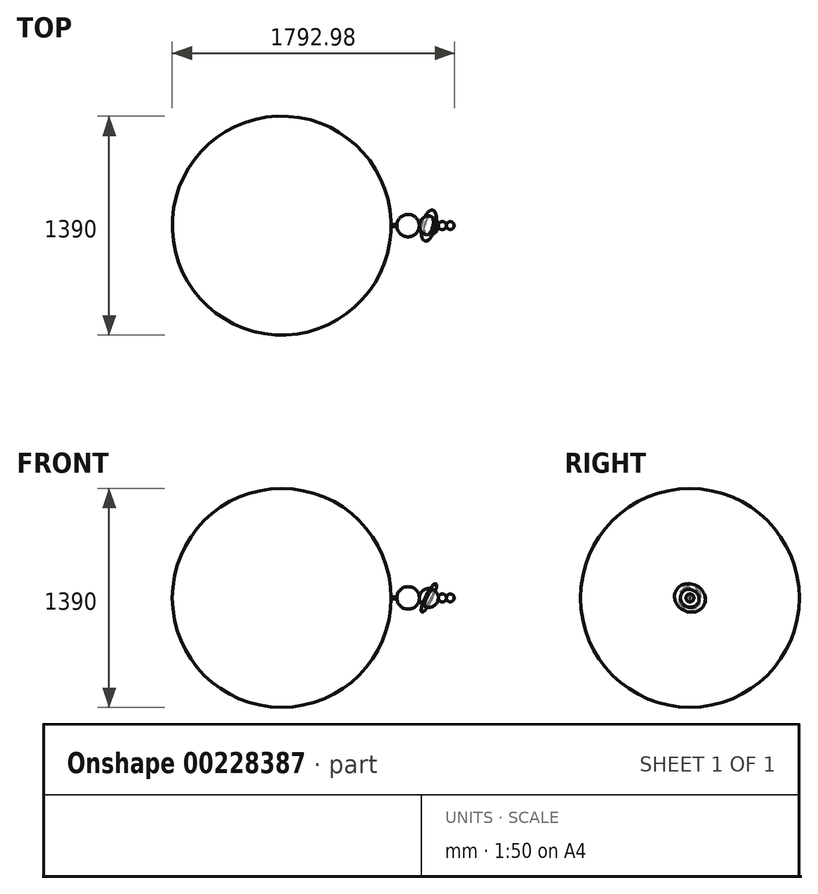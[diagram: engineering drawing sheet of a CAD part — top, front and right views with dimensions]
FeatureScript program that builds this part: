
annotation { "Feature Type Name" : "Feature", "Feature Type Description" : "" }
export const myFeature = defineFeature(function(context is Context, id is Id, definition is map)
    precondition{}
    {
        {
            assignVariable(context, id + "F0", {"name" : "SunD", "anyValue" : 1390});
        }
        {
            assignVariable(context, id + "F1", {"name" : "MercuryD", "anyValue" : 4.88});
        }
        {
            assignVariable(context, id + "F2", {"name" : "VenusD", "anyValue" : 12.1});
        }
        {
            assignVariable(context, id + "F3", {"name" : "EarthD", "anyValue" : 12.76});
        }
        {
            assignVariable(context, id + "F4", {"name" : "MarsD", "anyValue" : 6.8});
        }
        {
            assignVariable(context, id + "F5", {"name" : "JupiterD", "anyValue" : 143});
        }
        {
            assignVariable(context, id + "F6", {"name" : "SaturnD", "anyValue" : 120.5});
        }
        {
            assignVariable(context, id + "F7", {"name" : "UranusD", "anyValue" : 51.1});
        }
        {
            assignVariable(context, id + "F8", {"name" : "NeptuneD", "anyValue" : 49.5});
        }
        {
            assignVariable(context, id + "F9", {"name" : "PlutoD", "anyValue" : 2.35});
        }
        {
            var Q0;
            Q0=qCreatedBy(makeId("Top.planeOp"),FACE);
            var sketch = newSketch(context, id + "F10", { "sketchPlane" : qUnion([Q0])});
            skCircle(sketch, "E0", {"center": v(0, 0) * mm, "radius": 695 * mm});
            skCircle(sketch, "E1", {"center": v(0, 0) * mm, "radius": 2.44 * mm});
            skCircle(sketch, "E2", {"center": v(0, 0) * mm, "radius": 6.05 * mm});
            skCircle(sketch, "E3", {"center": v(0, 0) * mm, "radius": 6.38 * mm});
            skCircle(sketch, "E4", {"center": v(0, 0) * mm, "radius": 3.4 * mm});
            skCircle(sketch, "E5", {"center": v(0, 0) * mm, "radius": 71.5 * mm});
            skCircle(sketch, "E6", {"center": v(0, 0) * mm, "radius": 60.25 * mm});
            skCircle(sketch, "E7", {"center": v(0, 0) * mm, "radius": 25.55 * mm});
            skCircle(sketch, "E8", {"center": v(0, 0) * mm, "radius": 24.75 * mm});
            skCircle(sketch, "E9", {"center": v(0, 0) * mm, "radius": 1.18 * mm});
            skLineSegment(sketch, "E10", {"start": v(-694.4, -28.81) * mm, "end": v(0, 0) * mm});
            skLineSegment(sketch, "E11", {"start": v(0, 0) * mm, "end": v(694.4, 28.81) * mm});
            skCircle(sketch, "E12", {"center": v(0, 0) * mm, "radius": 100.25 * mm});
            skLineSegment(sketch, "E13", {"start": v(0, 0) * mm, "end": v(-4.16, 100.16) * mm, "construction": true});
            skSolve(sketch);
        }
        {
            var Q0;
            {var subQ0=sQuery(id+"F10.wireOp",EDGE,"E10");var subQ1=sQuery(id+"F10.wireOp",EDGE,"E1");var subQ2=makeQuery(id+"F10.imprint","INTERSECT",VERTEX,{"derivedFrom":[subQ1,subQ0]});Q0=makeQuery(id+"F10.imprint","IMPRINT",FACE,{"disambiguationData":[TD([[makeQuery(id+"F10.imprint","IMPRINT",EDGE,{"disambiguationData":[TD([[subQ2,1.0]])],"derivedFrom":subQ1}),1.0]])]});}
            var Q1;
            {var subQ0=sQuery(id+"F10.wireOp",EDGE,"E10");var subQ1=sQuery(id+"F10.wireOp",EDGE,"E9");var subQ2=makeQuery(id+"F10.imprint","INTERSECT",VERTEX,{"derivedFrom":[subQ1,subQ0]});Q1=makeQuery(id+"F10.imprint","IMPRINT",FACE,{"disambiguationData":[TD([[makeQuery(id+"F10.imprint","IMPRINT",EDGE,{"disambiguationData":[TD([[subQ2,1.0]])],"derivedFrom":subQ1}),1.0]])]});}
            var Q2;
            Q2=sQuery(id+"F10.wireOp",EDGE,"E10");
            revolve(context, id + "F11", {"entities" : qUnion([Q0, Q1]), "axis" : qUnion([Q2]), "revolveType" : RevolveType.FULL});
        }
        {
            var Q0;
            Q0=makeQuery(id+"F11.opRevolve","SWEPT_BODY",BODY,{"disambiguationData":[OSD([sQuery(id+"F10.wireOp",EDGE,"E1"),sQuery(id+"F10.wireOp",EDGE,"E10"),sQuery(id+"F10.wireOp",EDGE,"E11")])]});
            transform(context, id + "F12", {"entities" : qUnion([Q0]), "transformType" : TransformType.TRANSLATION_3D, "dx" : (getVariable(context, 'SunD') / 2 + getVariable(context, 'MercuryD') / 2) * mm, "dy" : 0 * mm, "dz" : 0 * mm, "makeCopy" : false});
        }
        {
            var Q0;
            {var subQ0=sQuery(id+"F10.wireOp",EDGE,"E10");var subQ1=sQuery(id+"F10.wireOp",EDGE,"E2");var subQ2=makeQuery(id+"F10.imprint","INTERSECT",VERTEX,{"derivedFrom":[subQ1,subQ0]});Q0=makeQuery(id+"F10.imprint","IMPRINT",FACE,{"disambiguationData":[TD([[makeQuery(id+"F10.imprint","IMPRINT",EDGE,{"disambiguationData":[TD([[subQ2,1.0]])],"derivedFrom":subQ1}),1.0]])]});}
            var Q1;
            {var subQ0=sQuery(id+"F10.wireOp",EDGE,"E10");var subQ1=sQuery(id+"F10.wireOp",EDGE,"E1");var subQ2=makeQuery(id+"F10.imprint","INTERSECT",VERTEX,{"derivedFrom":[subQ1,subQ0]});Q1=makeQuery(id+"F10.imprint","IMPRINT",FACE,{"disambiguationData":[TD([[makeQuery(id+"F10.imprint","IMPRINT",EDGE,{"disambiguationData":[TD([[subQ2,1.0]])],"derivedFrom":subQ1}),-1.0]])]});}
            var Q2;
            {var subQ0=sQuery(id+"F10.wireOp",EDGE,"E10");var subQ1=sQuery(id+"F10.wireOp",EDGE,"E1");var subQ2=makeQuery(id+"F10.imprint","INTERSECT",VERTEX,{"derivedFrom":[subQ1,subQ0]});Q2=makeQuery(id+"F10.imprint","IMPRINT",FACE,{"disambiguationData":[TD([[makeQuery(id+"F10.imprint","IMPRINT",EDGE,{"disambiguationData":[TD([[subQ2,1.0]])],"derivedFrom":subQ1}),1.0]])]});}
            var Q3;
            {var subQ0=sQuery(id+"F10.wireOp",EDGE,"E10");var subQ1=sQuery(id+"F10.wireOp",EDGE,"E9");var subQ2=makeQuery(id+"F10.imprint","INTERSECT",VERTEX,{"derivedFrom":[subQ1,subQ0]});Q3=makeQuery(id+"F10.imprint","IMPRINT",FACE,{"disambiguationData":[TD([[makeQuery(id+"F10.imprint","IMPRINT",EDGE,{"disambiguationData":[TD([[subQ2,1.0]])],"derivedFrom":subQ1}),1.0]])]});}
            var Q4;
            Q4=sQuery(id+"F10.wireOp",EDGE,"E11");
            revolve(context, id + "F13", {"entities" : qUnion([Q0, Q1, Q2, Q3]), "axis" : qUnion([Q4]), "revolveType" : RevolveType.FULL});
        }
        {
            var Q0;
            Q0=makeQuery(id+"F13.opRevolve","SWEPT_BODY",BODY,{"disambiguationData":[OSD([sQuery(id+"F10.wireOp",EDGE,"E2"),sQuery(id+"F10.wireOp",EDGE,"E10"),sQuery(id+"F10.wireOp",EDGE,"E11")])]});
            transform(context, id + "F14", {"entities" : qUnion([Q0]), "transformType" : TransformType.TRANSLATION_3D, "dx" : (getVariable(context, 'SunD') / 2 + getVariable(context, 'MercuryD') + getVariable(context, 'VenusD') / 2) * mm, "dy" : 0 * mm, "dz" : 0 * mm, "makeCopy" : false});
        }
        {
            var Q0;
            {var subQ0=sQuery(id+"F10.wireOp",EDGE,"E10");var subQ1=sQuery(id+"F10.wireOp",EDGE,"E2");var subQ2=makeQuery(id+"F10.imprint","INTERSECT",VERTEX,{"derivedFrom":[subQ1,subQ0]});Q0=makeQuery(id+"F10.imprint","IMPRINT",FACE,{"disambiguationData":[TD([[makeQuery(id+"F10.imprint","IMPRINT",EDGE,{"disambiguationData":[TD([[subQ2,1.0]])],"derivedFrom":subQ1}),-1.0]])]});}
            var Q1;
            {var subQ0=sQuery(id+"F10.wireOp",EDGE,"E10");var subQ1=sQuery(id+"F10.wireOp",EDGE,"E2");var subQ2=makeQuery(id+"F10.imprint","INTERSECT",VERTEX,{"derivedFrom":[subQ1,subQ0]});Q1=makeQuery(id+"F10.imprint","IMPRINT",FACE,{"disambiguationData":[TD([[makeQuery(id+"F10.imprint","IMPRINT",EDGE,{"disambiguationData":[TD([[subQ2,1.0]])],"derivedFrom":subQ1}),1.0]])]});}
            var Q2;
            {var subQ0=sQuery(id+"F10.wireOp",EDGE,"E10");var subQ1=sQuery(id+"F10.wireOp",EDGE,"E1");var subQ2=makeQuery(id+"F10.imprint","INTERSECT",VERTEX,{"derivedFrom":[subQ1,subQ0]});Q2=makeQuery(id+"F10.imprint","IMPRINT",FACE,{"disambiguationData":[TD([[makeQuery(id+"F10.imprint","IMPRINT",EDGE,{"disambiguationData":[TD([[subQ2,1.0]])],"derivedFrom":subQ1}),-1.0]])]});}
            var Q3;
            {var subQ0=sQuery(id+"F10.wireOp",EDGE,"E10");var subQ1=sQuery(id+"F10.wireOp",EDGE,"E1");var subQ2=makeQuery(id+"F10.imprint","INTERSECT",VERTEX,{"derivedFrom":[subQ1,subQ0]});Q3=makeQuery(id+"F10.imprint","IMPRINT",FACE,{"disambiguationData":[TD([[makeQuery(id+"F10.imprint","IMPRINT",EDGE,{"disambiguationData":[TD([[subQ2,1.0]])],"derivedFrom":subQ1}),1.0]])]});}
            var Q4;
            {var subQ0=sQuery(id+"F10.wireOp",EDGE,"E10");var subQ1=sQuery(id+"F10.wireOp",EDGE,"E9");var subQ2=makeQuery(id+"F10.imprint","INTERSECT",VERTEX,{"derivedFrom":[subQ1,subQ0]});Q4=makeQuery(id+"F10.imprint","IMPRINT",FACE,{"disambiguationData":[TD([[makeQuery(id+"F10.imprint","IMPRINT",EDGE,{"disambiguationData":[TD([[subQ2,1.0]])],"derivedFrom":subQ1}),1.0]])]});}
            var Q5;
            Q5=sQuery(id+"F10.wireOp",EDGE,"E10");
            revolve(context, id + "F15", {"entities" : qUnion([Q0, Q1, Q2, Q3, Q4]), "axis" : qUnion([Q5]), "revolveType" : RevolveType.FULL});
        }
        {
            var Q0;
            Q0=makeQuery(id+"F15.opRevolve","SWEPT_BODY",BODY,{"disambiguationData":[OSD([sQuery(id+"F10.wireOp",EDGE,"E3"),sQuery(id+"F10.wireOp",EDGE,"E10"),sQuery(id+"F10.wireOp",EDGE,"E11")])]});
            transform(context, id + "F16", {"entities" : qUnion([Q0]), "transformType" : TransformType.TRANSLATION_3D, "dx" : (getVariable(context, 'SunD') / 2 + getVariable(context, 'MercuryD') + getVariable(context, 'VenusD') + getVariable(context, 'EarthD') / 2) * mm, "dy" : 0 * mm, "dz" : 0 * mm, "makeCopy" : false});
        }
        {
            var Q0;
            {var subQ0=sQuery(id+"F10.wireOp",EDGE,"E10");var subQ1=sQuery(id+"F10.wireOp",EDGE,"E1");var subQ2=makeQuery(id+"F10.imprint","INTERSECT",VERTEX,{"derivedFrom":[subQ1,subQ0]});Q0=makeQuery(id+"F10.imprint","IMPRINT",FACE,{"disambiguationData":[TD([[makeQuery(id+"F10.imprint","IMPRINT",EDGE,{"disambiguationData":[TD([[subQ2,1.0]])],"derivedFrom":subQ1}),-1.0]])]});}
            var Q1;
            {var subQ0=sQuery(id+"F10.wireOp",EDGE,"E10");var subQ1=sQuery(id+"F10.wireOp",EDGE,"E1");var subQ2=makeQuery(id+"F10.imprint","INTERSECT",VERTEX,{"derivedFrom":[subQ1,subQ0]});Q1=makeQuery(id+"F10.imprint","IMPRINT",FACE,{"disambiguationData":[TD([[makeQuery(id+"F10.imprint","IMPRINT",EDGE,{"disambiguationData":[TD([[subQ2,1.0]])],"derivedFrom":subQ1}),1.0]])]});}
            var Q2;
            {var subQ0=sQuery(id+"F10.wireOp",EDGE,"E10");var subQ1=sQuery(id+"F10.wireOp",EDGE,"E9");var subQ2=makeQuery(id+"F10.imprint","INTERSECT",VERTEX,{"derivedFrom":[subQ1,subQ0]});Q2=makeQuery(id+"F10.imprint","IMPRINT",FACE,{"disambiguationData":[TD([[makeQuery(id+"F10.imprint","IMPRINT",EDGE,{"disambiguationData":[TD([[subQ2,1.0]])],"derivedFrom":subQ1}),1.0]])]});}
            var Q3;
            Q3=sQuery(id+"F10.wireOp",EDGE,"E11");
            revolve(context, id + "F17", {"entities" : qUnion([Q0, Q1, Q2]), "axis" : qUnion([Q3]), "revolveType" : RevolveType.FULL});
        }
        {
            var Q0;
            Q0=makeQuery(id+"F17.opRevolve","SWEPT_BODY",BODY,{"disambiguationData":[OSD([sQuery(id+"F10.wireOp",EDGE,"E4"),sQuery(id+"F10.wireOp",EDGE,"E10"),sQuery(id+"F10.wireOp",EDGE,"E11")])]});
            transform(context, id + "F18", {"entities" : qUnion([Q0]), "transformType" : TransformType.TRANSLATION_3D, "dx" : (getVariable(context, 'SunD') / 2 + getVariable(context, 'MercuryD') + getVariable(context, 'VenusD') + getVariable(context, 'EarthD') + getVariable(context, 'MarsD') / 2) * mm, "dy" : 0 * mm, "dz" : 0 * mm, "makeCopy" : false});
        }
        {
            var Q0;
            {var subQ0=sQuery(id+"F10.wireOp",EDGE,"E10");var subQ1=sQuery(id+"F10.wireOp",EDGE,"E5");var subQ2=makeQuery(id+"F10.imprint","INTERSECT",VERTEX,{"derivedFrom":[subQ1,subQ0]});Q0=makeQuery(id+"F10.imprint","IMPRINT",FACE,{"disambiguationData":[TD([[makeQuery(id+"F10.imprint","IMPRINT",EDGE,{"disambiguationData":[TD([[subQ2,1.0]])],"derivedFrom":subQ1}),1.0]])]});}
            var Q1;
            {var subQ0=sQuery(id+"F10.wireOp",EDGE,"E10");var subQ1=sQuery(id+"F10.wireOp",EDGE,"E6");var subQ2=makeQuery(id+"F10.imprint","INTERSECT",VERTEX,{"derivedFrom":[subQ1,subQ0]});Q1=makeQuery(id+"F10.imprint","IMPRINT",FACE,{"disambiguationData":[TD([[makeQuery(id+"F10.imprint","IMPRINT",EDGE,{"disambiguationData":[TD([[subQ2,1.0]])],"derivedFrom":subQ1}),1.0]])]});}
            var Q2;
            {var subQ0=sQuery(id+"F10.wireOp",EDGE,"E10");var subQ1=sQuery(id+"F10.wireOp",EDGE,"E3");var subQ2=makeQuery(id+"F10.imprint","INTERSECT",VERTEX,{"derivedFrom":[subQ1,subQ0]});Q2=makeQuery(id+"F10.imprint","IMPRINT",FACE,{"disambiguationData":[TD([[makeQuery(id+"F10.imprint","IMPRINT",EDGE,{"disambiguationData":[TD([[subQ2,1.0]])],"derivedFrom":subQ1}),-1.0]])]});}
            var Q3;
            {var subQ0=sQuery(id+"F10.wireOp",EDGE,"E10");var subQ1=sQuery(id+"F10.wireOp",EDGE,"E7");var subQ2=makeQuery(id+"F10.imprint","INTERSECT",VERTEX,{"derivedFrom":[subQ1,subQ0]});Q3=makeQuery(id+"F10.imprint","IMPRINT",FACE,{"disambiguationData":[TD([[makeQuery(id+"F10.imprint","IMPRINT",EDGE,{"disambiguationData":[TD([[subQ2,1.0]])],"derivedFrom":subQ1}),1.0]])]});}
            var Q4;
            {var subQ0=sQuery(id+"F10.wireOp",EDGE,"E10");var subQ1=sQuery(id+"F10.wireOp",EDGE,"E2");var subQ2=makeQuery(id+"F10.imprint","INTERSECT",VERTEX,{"derivedFrom":[subQ1,subQ0]});Q4=makeQuery(id+"F10.imprint","IMPRINT",FACE,{"disambiguationData":[TD([[makeQuery(id+"F10.imprint","IMPRINT",EDGE,{"disambiguationData":[TD([[subQ2,1.0]])],"derivedFrom":subQ1}),1.0]])]});}
            var Q5;
            {var subQ0=sQuery(id+"F10.wireOp",EDGE,"E10");var subQ1=sQuery(id+"F10.wireOp",EDGE,"E1");var subQ2=makeQuery(id+"F10.imprint","INTERSECT",VERTEX,{"derivedFrom":[subQ1,subQ0]});Q5=makeQuery(id+"F10.imprint","IMPRINT",FACE,{"disambiguationData":[TD([[makeQuery(id+"F10.imprint","IMPRINT",EDGE,{"disambiguationData":[TD([[subQ2,1.0]])],"derivedFrom":subQ1}),-1.0]])]});}
            var Q6;
            {var subQ0=sQuery(id+"F10.wireOp",EDGE,"E10");var subQ1=sQuery(id+"F10.wireOp",EDGE,"E1");var subQ2=makeQuery(id+"F10.imprint","INTERSECT",VERTEX,{"derivedFrom":[subQ1,subQ0]});Q6=makeQuery(id+"F10.imprint","IMPRINT",FACE,{"disambiguationData":[TD([[makeQuery(id+"F10.imprint","IMPRINT",EDGE,{"disambiguationData":[TD([[subQ2,1.0]])],"derivedFrom":subQ1}),1.0]])]});}
            var Q7;
            {var subQ0=sQuery(id+"F10.wireOp",EDGE,"E10");var subQ1=sQuery(id+"F10.wireOp",EDGE,"E9");var subQ2=makeQuery(id+"F10.imprint","INTERSECT",VERTEX,{"derivedFrom":[subQ1,subQ0]});Q7=makeQuery(id+"F10.imprint","IMPRINT",FACE,{"disambiguationData":[TD([[makeQuery(id+"F10.imprint","IMPRINT",EDGE,{"disambiguationData":[TD([[subQ2,1.0]])],"derivedFrom":subQ1}),1.0]])]});}
            var Q8;
            {var subQ0=sQuery(id+"F10.wireOp",EDGE,"E10");var subQ1=sQuery(id+"F10.wireOp",EDGE,"E2");var subQ2=makeQuery(id+"F10.imprint","INTERSECT",VERTEX,{"derivedFrom":[subQ1,subQ0]});Q8=makeQuery(id+"F10.imprint","IMPRINT",FACE,{"disambiguationData":[TD([[makeQuery(id+"F10.imprint","IMPRINT",EDGE,{"disambiguationData":[TD([[subQ2,1.0]])],"derivedFrom":subQ1}),-1.0]])]});}
            var Q9;
            Q9=sQuery(id+"F10.wireOp",EDGE,"E11");
            revolve(context, id + "F19", {"entities" : qUnion([Q0, Q1, Q2, Q3, Q4, Q5, Q6, Q7, Q8]), "axis" : qUnion([Q9]), "revolveType" : RevolveType.FULL});
        }
        {
            var Q0;
            Q0=makeQuery(id+"F19.opRevolve","SWEPT_BODY",BODY,{"disambiguationData":[OSD([sQuery(id+"F10.wireOp",EDGE,"E5"),sQuery(id+"F10.wireOp",EDGE,"E10"),sQuery(id+"F10.wireOp",EDGE,"E11")])]});
            transform(context, id + "F20", {"entities" : qUnion([Q0]), "transformType" : TransformType.TRANSLATION_3D, "dx" : (getVariable(context, 'SunD') / 2 + getVariable(context, 'MercuryD') + getVariable(context, 'VenusD') + getVariable(context, 'EarthD') + getVariable(context, 'MarsD') + getVariable(context, 'JupiterD') / 2) * mm, "dy" : 0 * mm, "dz" : 0 * mm, "makeCopy" : false});
        }
        {
            var Q0;
            {var subQ0=sQuery(id+"F10.wireOp",EDGE,"E10");var subQ1=sQuery(id+"F10.wireOp",EDGE,"E6");var subQ2=makeQuery(id+"F10.imprint","INTERSECT",VERTEX,{"derivedFrom":[subQ1,subQ0]});Q0=makeQuery(id+"F10.imprint","IMPRINT",FACE,{"disambiguationData":[TD([[makeQuery(id+"F10.imprint","IMPRINT",EDGE,{"disambiguationData":[TD([[subQ2,1.0]])],"derivedFrom":subQ1}),1.0]])]});}
            var Q1;
            {var subQ0=sQuery(id+"F10.wireOp",EDGE,"E10");var subQ1=sQuery(id+"F10.wireOp",EDGE,"E7");var subQ2=makeQuery(id+"F10.imprint","INTERSECT",VERTEX,{"derivedFrom":[subQ1,subQ0]});Q1=makeQuery(id+"F10.imprint","IMPRINT",FACE,{"disambiguationData":[TD([[makeQuery(id+"F10.imprint","IMPRINT",EDGE,{"disambiguationData":[TD([[subQ2,1.0]])],"derivedFrom":subQ1}),1.0]])]});}
            var Q2;
            {var subQ0=sQuery(id+"F10.wireOp",EDGE,"E10");var subQ1=sQuery(id+"F10.wireOp",EDGE,"E3");var subQ2=makeQuery(id+"F10.imprint","INTERSECT",VERTEX,{"derivedFrom":[subQ1,subQ0]});Q2=makeQuery(id+"F10.imprint","IMPRINT",FACE,{"disambiguationData":[TD([[makeQuery(id+"F10.imprint","IMPRINT",EDGE,{"disambiguationData":[TD([[subQ2,1.0]])],"derivedFrom":subQ1}),-1.0]])]});}
            var Q3;
            {var subQ0=sQuery(id+"F10.wireOp",EDGE,"E10");var subQ1=sQuery(id+"F10.wireOp",EDGE,"E2");var subQ2=makeQuery(id+"F10.imprint","INTERSECT",VERTEX,{"derivedFrom":[subQ1,subQ0]});Q3=makeQuery(id+"F10.imprint","IMPRINT",FACE,{"disambiguationData":[TD([[makeQuery(id+"F10.imprint","IMPRINT",EDGE,{"disambiguationData":[TD([[subQ2,1.0]])],"derivedFrom":subQ1}),1.0]])]});}
            var Q4;
            {var subQ0=sQuery(id+"F10.wireOp",EDGE,"E10");var subQ1=sQuery(id+"F10.wireOp",EDGE,"E1");var subQ2=makeQuery(id+"F10.imprint","INTERSECT",VERTEX,{"derivedFrom":[subQ1,subQ0]});Q4=makeQuery(id+"F10.imprint","IMPRINT",FACE,{"disambiguationData":[TD([[makeQuery(id+"F10.imprint","IMPRINT",EDGE,{"disambiguationData":[TD([[subQ2,1.0]])],"derivedFrom":subQ1}),-1.0]])]});}
            var Q5;
            {var subQ0=sQuery(id+"F10.wireOp",EDGE,"E10");var subQ1=sQuery(id+"F10.wireOp",EDGE,"E1");var subQ2=makeQuery(id+"F10.imprint","INTERSECT",VERTEX,{"derivedFrom":[subQ1,subQ0]});Q5=makeQuery(id+"F10.imprint","IMPRINT",FACE,{"disambiguationData":[TD([[makeQuery(id+"F10.imprint","IMPRINT",EDGE,{"disambiguationData":[TD([[subQ2,1.0]])],"derivedFrom":subQ1}),1.0]])]});}
            var Q6;
            {var subQ0=sQuery(id+"F10.wireOp",EDGE,"E10");var subQ1=sQuery(id+"F10.wireOp",EDGE,"E9");var subQ2=makeQuery(id+"F10.imprint","INTERSECT",VERTEX,{"derivedFrom":[subQ1,subQ0]});Q6=makeQuery(id+"F10.imprint","IMPRINT",FACE,{"disambiguationData":[TD([[makeQuery(id+"F10.imprint","IMPRINT",EDGE,{"disambiguationData":[TD([[subQ2,1.0]])],"derivedFrom":subQ1}),1.0]])]});}
            var Q7;
            {var subQ0=sQuery(id+"F10.wireOp",EDGE,"E10");var subQ1=sQuery(id+"F10.wireOp",EDGE,"E2");var subQ2=makeQuery(id+"F10.imprint","INTERSECT",VERTEX,{"derivedFrom":[subQ1,subQ0]});Q7=makeQuery(id+"F10.imprint","IMPRINT",FACE,{"disambiguationData":[TD([[makeQuery(id+"F10.imprint","IMPRINT",EDGE,{"disambiguationData":[TD([[subQ2,1.0]])],"derivedFrom":subQ1}),-1.0]])]});}
            var Q8;
            Q8=sQuery(id+"F10.wireOp",EDGE,"E10");
            revolve(context, id + "F21", {"entities" : qUnion([Q0, Q1, Q2, Q3, Q4, Q5, Q6, Q7]), "axis" : qUnion([Q8]), "revolveType" : RevolveType.FULL});
        }
        {
            var Q0;
            {var subQ0=sQuery(id+"F10.wireOp",EDGE,"E10");var subQ1=sQuery(id+"F10.wireOp",EDGE,"E5");var subQ2=makeQuery(id+"F10.imprint","INTERSECT",VERTEX,{"derivedFrom":[subQ1,subQ0]});Q0=makeQuery(id+"F10.imprint","IMPRINT",FACE,{"disambiguationData":[TD([[makeQuery(id+"F10.imprint","IMPRINT",EDGE,{"disambiguationData":[TD([[subQ2,1.0]])],"derivedFrom":subQ1}),-1.0]])]});}
            var Q1;
            {var subQ0=sQuery(id+"F10.wireOp",EDGE,"E10");var subQ1=sQuery(id+"F10.wireOp",EDGE,"E5");var subQ2=makeQuery(id+"F10.imprint","INTERSECT",VERTEX,{"derivedFrom":[subQ1,subQ0]});Q1=makeQuery(id+"F10.imprint","IMPRINT",FACE,{"disambiguationData":[TD([[makeQuery(id+"F10.imprint","IMPRINT",EDGE,{"disambiguationData":[TD([[subQ2,1.0]])],"derivedFrom":subQ1}),1.0]])]});}
            var Q2;
            {var subQ0=sQuery(id+"F10.wireOp",EDGE,"E10");var subQ1=sQuery(id+"F10.wireOp",EDGE,"E5");var subQ2=makeQuery(id+"F10.imprint","INTERSECT",VERTEX,{"derivedFrom":[subQ1,subQ0]});Q2=makeQuery(id+"F10.imprint","IMPRINT",FACE,{"disambiguationData":[TD([[makeQuery(id+"F10.imprint","IMPRINT",EDGE,{"disambiguationData":[TD([[subQ2,-1.0]])],"derivedFrom":subQ1}),1.0]])]});}
            var Q3;
            {var subQ0=sQuery(id+"F10.wireOp",EDGE,"E10");var subQ1=sQuery(id+"F10.wireOp",EDGE,"E5");var subQ2=makeQuery(id+"F10.imprint","INTERSECT",VERTEX,{"derivedFrom":[subQ1,subQ0]});Q3=makeQuery(id+"F10.imprint","IMPRINT",FACE,{"disambiguationData":[TD([[makeQuery(id+"F10.imprint","IMPRINT",EDGE,{"disambiguationData":[TD([[subQ2,-1.0]])],"derivedFrom":subQ1}),-1.0]])]});}
            extrude(context, id + "F22", {"entities" : qUnion([Q0, Q1, Q2, Q3]), "operationType" : NewBodyOperationType.ADD, "depth" : 0.5 * mm});
        }
        {
            var Q0;
            {var subQ0=sQuery(id+"F10.wireOp",EDGE,"E10");var subQ1=sQuery(id+"F10.wireOp",EDGE,"E5");var subQ2=makeQuery(id+"F10.imprint","INTERSECT",VERTEX,{"derivedFrom":[subQ1,subQ0]});Q0=makeQuery(id+"F10.imprint","IMPRINT",FACE,{"disambiguationData":[TD([[makeQuery(id+"F10.imprint","IMPRINT",EDGE,{"disambiguationData":[TD([[subQ2,1.0]])],"derivedFrom":subQ1}),-1.0]])]});}
            var Q1;
            {var subQ0=sQuery(id+"F10.wireOp",EDGE,"E10");var subQ1=sQuery(id+"F10.wireOp",EDGE,"E5");var subQ2=makeQuery(id+"F10.imprint","INTERSECT",VERTEX,{"derivedFrom":[subQ1,subQ0]});Q1=makeQuery(id+"F10.imprint","IMPRINT",FACE,{"disambiguationData":[TD([[makeQuery(id+"F10.imprint","IMPRINT",EDGE,{"disambiguationData":[TD([[subQ2,1.0]])],"derivedFrom":subQ1}),1.0]])]});}
            var Q2;
            {var subQ0=sQuery(id+"F10.wireOp",EDGE,"E10");var subQ1=sQuery(id+"F10.wireOp",EDGE,"E5");var subQ2=makeQuery(id+"F10.imprint","INTERSECT",VERTEX,{"derivedFrom":[subQ1,subQ0]});Q2=makeQuery(id+"F10.imprint","IMPRINT",FACE,{"disambiguationData":[TD([[makeQuery(id+"F10.imprint","IMPRINT",EDGE,{"disambiguationData":[TD([[subQ2,-1.0]])],"derivedFrom":subQ1}),-1.0]])]});}
            var Q3;
            {var subQ0=sQuery(id+"F10.wireOp",EDGE,"E10");var subQ1=sQuery(id+"F10.wireOp",EDGE,"E5");var subQ2=makeQuery(id+"F10.imprint","INTERSECT",VERTEX,{"derivedFrom":[subQ1,subQ0]});Q3=makeQuery(id+"F10.imprint","IMPRINT",FACE,{"disambiguationData":[TD([[makeQuery(id+"F10.imprint","IMPRINT",EDGE,{"disambiguationData":[TD([[subQ2,-1.0]])],"derivedFrom":subQ1}),1.0]])]});}
            extrude(context, id + "F23", {"entities" : qUnion([Q0, Q1, Q2, Q3]), "operationType" : NewBodyOperationType.ADD, "oppositeDirection" : true, "depth" : 0.5 * mm});
        }
        {
            var Q0;
            Q0=makeQuery(id+"F21.opRevolve","SWEPT_BODY",BODY,{"disambiguationData":[OSD([sQuery(id+"F10.wireOp",EDGE,"E6"),sQuery(id+"F10.wireOp",EDGE,"E10"),sQuery(id+"F10.wireOp",EDGE,"E11")])]});
            var Q1;
            Q1=sQuery(id+"F10.wireOp",EDGE,"E13");
            transform(context, id + "F24", {"entities" : qUnion([Q0]), "transformType" : TransformType.ROTATION, "transformAxis" : qUnion([Q1]), "angle" : 120 * degree, "makeCopy" : false});
        }
        {
            var Q0;
            Q0=makeQuery(id+"F21.opRevolve","SWEPT_BODY",BODY,{"disambiguationData":[OSD([sQuery(id+"F10.wireOp",EDGE,"E6"),sQuery(id+"F10.wireOp",EDGE,"E10"),sQuery(id+"F10.wireOp",EDGE,"E11")])]});
            var Q1;
            Q1=sQuery(id+"F10.wireOp",EDGE,"E10");
            transform(context, id + "F25", {"entities" : qUnion([Q0]), "transformType" : TransformType.ROTATION, "transformAxis" : qUnion([Q1]), "angle" : 30 * degree, "oppositeDirection" : true, "makeCopy" : false});
        }
        {
            var Q0;
            Q0=makeQuery(id+"F21.opRevolve","SWEPT_BODY",BODY,{"disambiguationData":[OSD([sQuery(id+"F10.wireOp",EDGE,"E6"),sQuery(id+"F10.wireOp",EDGE,"E10"),sQuery(id+"F10.wireOp",EDGE,"E11")])]});
            transform(context, id + "F26", {"entities" : qUnion([Q0]), "transformType" : TransformType.TRANSLATION_3D, "dx" : (getVariable(context, 'SunD') / 2 + getVariable(context, 'MercuryD') + getVariable(context, 'VenusD') + getVariable(context, 'EarthD') + getVariable(context, 'MarsD') + getVariable(context, 'JupiterD') + getVariable(context, 'SaturnD') / 2) * mm, "dy" : 0 * mm, "dz" : 0 * mm, "makeCopy" : false});
        }
        {
            var Q0;
            {var subQ0=sQuery(id+"F10.wireOp",EDGE,"E10");var subQ1=sQuery(id+"F10.wireOp",EDGE,"E3");var subQ2=makeQuery(id+"F10.imprint","INTERSECT",VERTEX,{"derivedFrom":[subQ1,subQ0]});Q0=makeQuery(id+"F10.imprint","IMPRINT",FACE,{"disambiguationData":[TD([[makeQuery(id+"F10.imprint","IMPRINT",EDGE,{"disambiguationData":[TD([[subQ2,1.0]])],"derivedFrom":subQ1}),-1.0]])]});}
            var Q1;
            {var subQ0=sQuery(id+"F10.wireOp",EDGE,"E10");var subQ1=sQuery(id+"F10.wireOp",EDGE,"E2");var subQ2=makeQuery(id+"F10.imprint","INTERSECT",VERTEX,{"derivedFrom":[subQ1,subQ0]});Q1=makeQuery(id+"F10.imprint","IMPRINT",FACE,{"disambiguationData":[TD([[makeQuery(id+"F10.imprint","IMPRINT",EDGE,{"disambiguationData":[TD([[subQ2,1.0]])],"derivedFrom":subQ1}),1.0]])]});}
            var Q2;
            {var subQ0=sQuery(id+"F10.wireOp",EDGE,"E10");var subQ1=sQuery(id+"F10.wireOp",EDGE,"E1");var subQ2=makeQuery(id+"F10.imprint","INTERSECT",VERTEX,{"derivedFrom":[subQ1,subQ0]});Q2=makeQuery(id+"F10.imprint","IMPRINT",FACE,{"disambiguationData":[TD([[makeQuery(id+"F10.imprint","IMPRINT",EDGE,{"disambiguationData":[TD([[subQ2,1.0]])],"derivedFrom":subQ1}),-1.0]])]});}
            var Q3;
            {var subQ0=sQuery(id+"F10.wireOp",EDGE,"E10");var subQ1=sQuery(id+"F10.wireOp",EDGE,"E1");var subQ2=makeQuery(id+"F10.imprint","INTERSECT",VERTEX,{"derivedFrom":[subQ1,subQ0]});Q3=makeQuery(id+"F10.imprint","IMPRINT",FACE,{"disambiguationData":[TD([[makeQuery(id+"F10.imprint","IMPRINT",EDGE,{"disambiguationData":[TD([[subQ2,1.0]])],"derivedFrom":subQ1}),1.0]])]});}
            var Q4;
            {var subQ0=sQuery(id+"F10.wireOp",EDGE,"E10");var subQ1=sQuery(id+"F10.wireOp",EDGE,"E9");var subQ2=makeQuery(id+"F10.imprint","INTERSECT",VERTEX,{"derivedFrom":[subQ1,subQ0]});Q4=makeQuery(id+"F10.imprint","IMPRINT",FACE,{"disambiguationData":[TD([[makeQuery(id+"F10.imprint","IMPRINT",EDGE,{"disambiguationData":[TD([[subQ2,1.0]])],"derivedFrom":subQ1}),1.0]])]});}
            var Q5;
            {var subQ0=sQuery(id+"F10.wireOp",EDGE,"E10");var subQ1=sQuery(id+"F10.wireOp",EDGE,"E2");var subQ2=makeQuery(id+"F10.imprint","INTERSECT",VERTEX,{"derivedFrom":[subQ1,subQ0]});Q5=makeQuery(id+"F10.imprint","IMPRINT",FACE,{"disambiguationData":[TD([[makeQuery(id+"F10.imprint","IMPRINT",EDGE,{"disambiguationData":[TD([[subQ2,1.0]])],"derivedFrom":subQ1}),-1.0]])]});}
            var Q6;
            {var subQ0=sQuery(id+"F10.wireOp",EDGE,"E10");var subQ1=sQuery(id+"F10.wireOp",EDGE,"E7");var subQ2=makeQuery(id+"F10.imprint","INTERSECT",VERTEX,{"derivedFrom":[subQ1,subQ0]});Q6=makeQuery(id+"F10.imprint","IMPRINT",FACE,{"disambiguationData":[TD([[makeQuery(id+"F10.imprint","IMPRINT",EDGE,{"disambiguationData":[TD([[subQ2,1.0]])],"derivedFrom":subQ1}),1.0]])]});}
            var Q7;
            Q7=sQuery(id+"F10.wireOp",EDGE,"E10");
            revolve(context, id + "F27", {"entities" : qUnion([Q0, Q1, Q2, Q3, Q4, Q5, Q6]), "axis" : qUnion([Q7]), "revolveType" : RevolveType.FULL});
        }
        {
            var Q0;
            Q0=makeQuery(id+"F27.opRevolve","SWEPT_BODY",BODY,{"disambiguationData":[OSD([sQuery(id+"F10.wireOp",EDGE,"E7"),sQuery(id+"F10.wireOp",EDGE,"E10"),sQuery(id+"F10.wireOp",EDGE,"E11")])]});
            transform(context, id + "F28", {"entities" : qUnion([Q0]), "transformType" : TransformType.TRANSLATION_3D, "dx" : (getVariable(context, 'SunD') / 2 + getVariable(context, 'MercuryD') + getVariable(context, 'VenusD') + getVariable(context, 'EarthD') + getVariable(context, 'MarsD') + getVariable(context, 'JupiterD') + getVariable(context, 'SaturnD') + getVariable(context, 'UranusD') / 2) * mm, "dy" : 0 * mm, "dz" : 0 * mm, "makeCopy" : false});
        }
        {
            var Q0;
            {var subQ0=sQuery(id+"F10.wireOp",EDGE,"E10");var subQ1=sQuery(id+"F10.wireOp",EDGE,"E9");var subQ2=makeQuery(id+"F10.imprint","INTERSECT",VERTEX,{"derivedFrom":[subQ1,subQ0]});Q0=makeQuery(id+"F10.imprint","IMPRINT",FACE,{"disambiguationData":[TD([[makeQuery(id+"F10.imprint","IMPRINT",EDGE,{"disambiguationData":[TD([[subQ2,1.0]])],"derivedFrom":subQ1}),1.0]])]});}
            var Q1;
            {var subQ0=sQuery(id+"F10.wireOp",EDGE,"E10");var subQ1=sQuery(id+"F10.wireOp",EDGE,"E1");var subQ2=makeQuery(id+"F10.imprint","INTERSECT",VERTEX,{"derivedFrom":[subQ1,subQ0]});Q1=makeQuery(id+"F10.imprint","IMPRINT",FACE,{"disambiguationData":[TD([[makeQuery(id+"F10.imprint","IMPRINT",EDGE,{"disambiguationData":[TD([[subQ2,1.0]])],"derivedFrom":subQ1}),1.0]])]});}
            var Q2;
            {var subQ0=sQuery(id+"F10.wireOp",EDGE,"E10");var subQ1=sQuery(id+"F10.wireOp",EDGE,"E1");var subQ2=makeQuery(id+"F10.imprint","INTERSECT",VERTEX,{"derivedFrom":[subQ1,subQ0]});Q2=makeQuery(id+"F10.imprint","IMPRINT",FACE,{"disambiguationData":[TD([[makeQuery(id+"F10.imprint","IMPRINT",EDGE,{"disambiguationData":[TD([[subQ2,1.0]])],"derivedFrom":subQ1}),-1.0]])]});}
            var Q3;
            {var subQ0=sQuery(id+"F10.wireOp",EDGE,"E10");var subQ1=sQuery(id+"F10.wireOp",EDGE,"E2");var subQ2=makeQuery(id+"F10.imprint","INTERSECT",VERTEX,{"derivedFrom":[subQ1,subQ0]});Q3=makeQuery(id+"F10.imprint","IMPRINT",FACE,{"disambiguationData":[TD([[makeQuery(id+"F10.imprint","IMPRINT",EDGE,{"disambiguationData":[TD([[subQ2,1.0]])],"derivedFrom":subQ1}),1.0]])]});}
            var Q4;
            {var subQ0=sQuery(id+"F10.wireOp",EDGE,"E10");var subQ1=sQuery(id+"F10.wireOp",EDGE,"E2");var subQ2=makeQuery(id+"F10.imprint","INTERSECT",VERTEX,{"derivedFrom":[subQ1,subQ0]});Q4=makeQuery(id+"F10.imprint","IMPRINT",FACE,{"disambiguationData":[TD([[makeQuery(id+"F10.imprint","IMPRINT",EDGE,{"disambiguationData":[TD([[subQ2,1.0]])],"derivedFrom":subQ1}),-1.0]])]});}
            var Q5;
            {var subQ0=sQuery(id+"F10.wireOp",EDGE,"E10");var subQ1=sQuery(id+"F10.wireOp",EDGE,"E3");var subQ2=makeQuery(id+"F10.imprint","INTERSECT",VERTEX,{"derivedFrom":[subQ1,subQ0]});Q5=makeQuery(id+"F10.imprint","IMPRINT",FACE,{"disambiguationData":[TD([[makeQuery(id+"F10.imprint","IMPRINT",EDGE,{"disambiguationData":[TD([[subQ2,1.0]])],"derivedFrom":subQ1}),-1.0]])]});}
            var Q6;
            Q6=sQuery(id+"F10.wireOp",EDGE,"E10");
            revolve(context, id + "F29", {"entities" : qUnion([Q0, Q1, Q2, Q3, Q4, Q5]), "axis" : qUnion([Q6]), "revolveType" : RevolveType.FULL});
        }
        {
            var Q0;
            Q0=makeQuery(id+"F29.opRevolve","SWEPT_BODY",BODY,{"disambiguationData":[OSD([sQuery(id+"F10.wireOp",EDGE,"E8"),sQuery(id+"F10.wireOp",EDGE,"E10"),sQuery(id+"F10.wireOp",EDGE,"E11")])]});
            transform(context, id + "F30", {"entities" : qUnion([Q0]), "transformType" : TransformType.TRANSLATION_3D, "dx" : (getVariable(context, 'SunD') / 2 + getVariable(context, 'MercuryD') + getVariable(context, 'VenusD') + getVariable(context, 'EarthD') + getVariable(context, 'MarsD') + getVariable(context, 'JupiterD') + getVariable(context, 'SaturnD') + getVariable(context, 'UranusD') + getVariable(context, 'NeptuneD') / 2) * mm, "dy" : 0 * mm, "dz" : 0 * mm, "makeCopy" : false});
        }
        {
            var Q0;
            {var subQ0=sQuery(id+"F10.wireOp",EDGE,"E10");var subQ1=sQuery(id+"F10.wireOp",EDGE,"E9");var subQ2=makeQuery(id+"F10.imprint","INTERSECT",VERTEX,{"derivedFrom":[subQ1,subQ0]});Q0=makeQuery(id+"F10.imprint","IMPRINT",FACE,{"disambiguationData":[TD([[makeQuery(id+"F10.imprint","IMPRINT",EDGE,{"disambiguationData":[TD([[subQ2,1.0]])],"derivedFrom":subQ1}),1.0]])]});}
            var Q1;
            Q1=sQuery(id+"F10.wireOp",EDGE,"E10");
            revolve(context, id + "F31", {"entities" : qUnion([Q0]), "axis" : qUnion([Q1]), "revolveType" : RevolveType.FULL});
        }
        {
            var Q0;
            Q0=makeQuery(id+"F31.opRevolve","SWEPT_BODY",BODY,{"disambiguationData":[OSD([sQuery(id+"F10.wireOp",EDGE,"E9"),sQuery(id+"F10.wireOp",EDGE,"E10"),sQuery(id+"F10.wireOp",EDGE,"E11")])]});
            transform(context, id + "F32", {"entities" : qUnion([Q0]), "transformType" : TransformType.TRANSLATION_3D, "dx" : (getVariable(context, 'SunD') / 2 + getVariable(context, 'MercuryD') + getVariable(context, 'VenusD') + getVariable(context, 'EarthD') + getVariable(context, 'MarsD') + getVariable(context, 'JupiterD') + getVariable(context, 'SaturnD') + getVariable(context, 'UranusD') + getVariable(context, 'NeptuneD') + getVariable(context, 'PlutoD') / 2) * mm, "dy" : 0 * mm, "dz" : 0 * mm, "makeCopy" : false});
        }
        {
            var Q0;
            {var subQ0=sQuery(id+"F10.wireOp",EDGE,"E10");var subQ1=sQuery(id+"F10.wireOp",EDGE,"E0");var subQ2=makeQuery(id+"F10.imprint","INTERSECT",VERTEX,{"derivedFrom":[subQ1,subQ0]});Q0=makeQuery(id+"F10.imprint","IMPRINT",FACE,{"disambiguationData":[TD([[makeQuery(id+"F10.imprint","IMPRINT",EDGE,{"disambiguationData":[TD([[subQ2,1.0]])],"derivedFrom":subQ1}),1.0]])]});}
            var Q1;
            {var subQ0=sQuery(id+"F10.wireOp",EDGE,"E10");var subQ1=sQuery(id+"F10.wireOp",EDGE,"E5");var subQ2=makeQuery(id+"F10.imprint","INTERSECT",VERTEX,{"derivedFrom":[subQ1,subQ0]});Q1=makeQuery(id+"F10.imprint","IMPRINT",FACE,{"disambiguationData":[TD([[makeQuery(id+"F10.imprint","IMPRINT",EDGE,{"disambiguationData":[TD([[subQ2,1.0]])],"derivedFrom":subQ1}),-1.0]])]});}
            var Q2;
            {var subQ0=sQuery(id+"F10.wireOp",EDGE,"E10");var subQ1=sQuery(id+"F10.wireOp",EDGE,"E5");var subQ2=makeQuery(id+"F10.imprint","INTERSECT",VERTEX,{"derivedFrom":[subQ1,subQ0]});Q2=makeQuery(id+"F10.imprint","IMPRINT",FACE,{"disambiguationData":[TD([[makeQuery(id+"F10.imprint","IMPRINT",EDGE,{"disambiguationData":[TD([[subQ2,1.0]])],"derivedFrom":subQ1}),1.0]])]});}
            var Q3;
            {var subQ0=sQuery(id+"F10.wireOp",EDGE,"E10");var subQ1=sQuery(id+"F10.wireOp",EDGE,"E6");var subQ2=makeQuery(id+"F10.imprint","INTERSECT",VERTEX,{"derivedFrom":[subQ1,subQ0]});Q3=makeQuery(id+"F10.imprint","IMPRINT",FACE,{"disambiguationData":[TD([[makeQuery(id+"F10.imprint","IMPRINT",EDGE,{"disambiguationData":[TD([[subQ2,1.0]])],"derivedFrom":subQ1}),1.0]])]});}
            var Q4;
            {var subQ0=sQuery(id+"F10.wireOp",EDGE,"E10");var subQ1=sQuery(id+"F10.wireOp",EDGE,"E7");var subQ2=makeQuery(id+"F10.imprint","INTERSECT",VERTEX,{"derivedFrom":[subQ1,subQ0]});Q4=makeQuery(id+"F10.imprint","IMPRINT",FACE,{"disambiguationData":[TD([[makeQuery(id+"F10.imprint","IMPRINT",EDGE,{"disambiguationData":[TD([[subQ2,1.0]])],"derivedFrom":subQ1}),1.0]])]});}
            var Q5;
            {var subQ0=sQuery(id+"F10.wireOp",EDGE,"E10");var subQ1=sQuery(id+"F10.wireOp",EDGE,"E3");var subQ2=makeQuery(id+"F10.imprint","INTERSECT",VERTEX,{"derivedFrom":[subQ1,subQ0]});Q5=makeQuery(id+"F10.imprint","IMPRINT",FACE,{"disambiguationData":[TD([[makeQuery(id+"F10.imprint","IMPRINT",EDGE,{"disambiguationData":[TD([[subQ2,1.0]])],"derivedFrom":subQ1}),-1.0]])]});}
            var Q6;
            {var subQ0=sQuery(id+"F10.wireOp",EDGE,"E10");var subQ1=sQuery(id+"F10.wireOp",EDGE,"E2");var subQ2=makeQuery(id+"F10.imprint","INTERSECT",VERTEX,{"derivedFrom":[subQ1,subQ0]});Q6=makeQuery(id+"F10.imprint","IMPRINT",FACE,{"disambiguationData":[TD([[makeQuery(id+"F10.imprint","IMPRINT",EDGE,{"disambiguationData":[TD([[subQ2,1.0]])],"derivedFrom":subQ1}),-1.0]])]});}
            var Q7;
            {var subQ0=sQuery(id+"F10.wireOp",EDGE,"E10");var subQ1=sQuery(id+"F10.wireOp",EDGE,"E2");var subQ2=makeQuery(id+"F10.imprint","INTERSECT",VERTEX,{"derivedFrom":[subQ1,subQ0]});Q7=makeQuery(id+"F10.imprint","IMPRINT",FACE,{"disambiguationData":[TD([[makeQuery(id+"F10.imprint","IMPRINT",EDGE,{"disambiguationData":[TD([[subQ2,1.0]])],"derivedFrom":subQ1}),1.0]])]});}
            var Q8;
            {var subQ0=sQuery(id+"F10.wireOp",EDGE,"E10");var subQ1=sQuery(id+"F10.wireOp",EDGE,"E1");var subQ2=makeQuery(id+"F10.imprint","INTERSECT",VERTEX,{"derivedFrom":[subQ1,subQ0]});Q8=makeQuery(id+"F10.imprint","IMPRINT",FACE,{"disambiguationData":[TD([[makeQuery(id+"F10.imprint","IMPRINT",EDGE,{"disambiguationData":[TD([[subQ2,1.0]])],"derivedFrom":subQ1}),-1.0]])]});}
            var Q9;
            {var subQ0=sQuery(id+"F10.wireOp",EDGE,"E10");var subQ1=sQuery(id+"F10.wireOp",EDGE,"E1");var subQ2=makeQuery(id+"F10.imprint","INTERSECT",VERTEX,{"derivedFrom":[subQ1,subQ0]});Q9=makeQuery(id+"F10.imprint","IMPRINT",FACE,{"disambiguationData":[TD([[makeQuery(id+"F10.imprint","IMPRINT",EDGE,{"disambiguationData":[TD([[subQ2,1.0]])],"derivedFrom":subQ1}),1.0]])]});}
            var Q10;
            {var subQ0=sQuery(id+"F10.wireOp",EDGE,"E10");var subQ1=sQuery(id+"F10.wireOp",EDGE,"E9");var subQ2=makeQuery(id+"F10.imprint","INTERSECT",VERTEX,{"derivedFrom":[subQ1,subQ0]});Q10=makeQuery(id+"F10.imprint","IMPRINT",FACE,{"disambiguationData":[TD([[makeQuery(id+"F10.imprint","IMPRINT",EDGE,{"disambiguationData":[TD([[subQ2,1.0]])],"derivedFrom":subQ1}),1.0]])]});}
            var Q11;
            Q11=sQuery(id+"F10.wireOp",EDGE,"E10");
            revolve(context, id + "F33", {"entities" : qUnion([Q0, Q1, Q2, Q3, Q4, Q5, Q6, Q7, Q8, Q9, Q10]), "axis" : qUnion([Q11]), "revolveType" : RevolveType.FULL});
        }
    });
